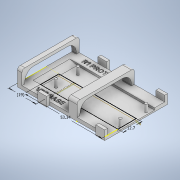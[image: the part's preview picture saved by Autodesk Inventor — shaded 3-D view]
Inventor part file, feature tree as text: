
AUTODESK INVENTOR PART (.ipt)
format: ipt  version: 2021 (Build 250183000, 183)  size: 1,393,664 bytes
history: native  units: in
note: dims shown in document units (in); Inventor stores cm internally (conversion verified against a paired STEP export)
features: sketch x13, extrude x9, plane x2, mirror x2, fillet x2, chamfer x1
ambient origin geometry x8: Origin, YZ Plane, XZ Plane, XY Plane, X Axis, Y Axis, Z Axis, Center Point
bodies: Solid1 (feature_tree)
feature tree (29):
  extrude  "Extrusion1"  Depth=0.7756in
  sketch  "Sketch2"  dims[d7=0.0945in d8=0.0in d9=0.2362in]
  extrude  "Extrusion2"  Depth=0.2362in
  plane  "Work Plane1"
  extrude  "Extrusion3"  Depth=0.2362in
  sketch  "Sketch5"  dims[d16=0.1575in d17=0.0in d18=0.2362in]
  extrude  "Extrusion4"  TaperAngle=0.0deg  [1 undecoded]
  sketch  "Sketch7"  dims[d23=0.378in d24=0.6969in]
  extrude  "Extrusion5"  Depth=0.2362in
  sketch  "Sketch9"  dims[d27=0.0in]
  plane  "Work Plane2"
  mirror  "Mirror2"
  extrude  "Extrusion8"  Depth=0.378in
  fillet  "Fillet3"  [1 undecoded]
  fillet  "Fillet4"  Radius=0.7756in
  extrude  "Extrusion9"  Depth=0.6969in
  mirror  "Mirror3"
  extrude  "Extrusion10"  Depth=1.4803in
  chamfer  "Chamfer1"  Distance=0.0551in
  extrude  "Extrusion11"  Depth=0.0787in
  sketch  "Sketch1"  dims[d5=2.4409in d6=0.7756in]
  sketch  "Sketch3"  dims[d10=0.0787in d11=0.0in d13=0.2362in]
  sketch  "Sketch4"  dims[d14=1.3386in d15=0.0in]
  sketch  "Sketch6"  dims[d19=0.8268in d20=0.378in d21=0.0in d22=0.7756in]
  sketch  "Sketch8"  dims[d25=0.2992in d26=1.4803in]
  sketch  "Sketch12"  dims[d29=-0.748in]
  sketch  "Sketch13"  dims[d30=0.748in]
  sketch  "Sketch14"  dims[d41=2.1in]
  sketch  "Sketch15"  dims[d42=0.5in d43=0.0551in d44=0.0in d46=0.0787in d47=0.2756in d48=0.0709in d49=0.0709in d50=1.8in d51=0.35in d52=0.1969in d53=0.0in d54=0.1969in d55=0.0in d56=0.1969in d57=0.0551in d58=45.0deg d59=0.0787in d60=0.0787in d61=0.0394in d62=0.0394in d63=0.0394in d64=0.0394in d65=0.0787in d66=0.0787in d67=0.0394in d68=0.0in]
note: 2 required parameter values undecoded (feature->parameter linkage not recoverable at this tier; creation-order binding heuristic only, values carry confidence <= 0.55)
